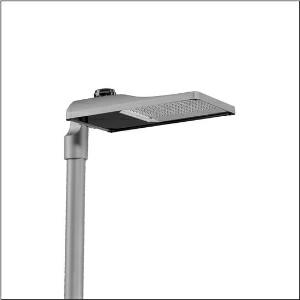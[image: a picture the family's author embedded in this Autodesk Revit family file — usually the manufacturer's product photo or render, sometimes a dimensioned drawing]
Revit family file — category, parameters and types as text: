
# Revit family: streetlight_sl_31_maxi___pl52_5xh8h75n08sa_385d
name_source: partatom
category: Lighting Fixtures
units: mm (PartAtom-declared; Revit-internal decimal feet)

## family parameters
Cut with Voids When Loaded = No
Host = Face
Light Source = No
Part Type = Normal
Room Calculation Point = No
Round Connector Dimension = Use Diameter
Shared = No

## types (1)
- --- (1 x LED, 22470 lm, 208.6 W, 2200K)
    Apparent Load = 209 VA
    CIE Flux Codes = 27 59 98 100 100
    Color Rendering = 70
    Color Temperature = 2200K
    Default Elevation = 1800 mm
    Description = Streetlight SL 31 maxi, mast luminaire, primary light control with lens, of PMMA, primary optical cover: cover, of toughened safety glass, transparent, light distribution: PL52, light emission: direct distribution, primary light characteristic: asymmetric, installation type: post-top, side-entry, LED, High Power LED, rated luminous flux: 22.470lm, luminous efficacy: 108lm/W, light colour: 722, colour temperature: 2200K, control: presetting dimming linear, flexible luminous flux parameterisation, time-dependent luminous flux control, constant luminous flux control, intelligent temperature release in ECG and LED module, overheat protection, with cable H07RN-F 3x 1.5mm², mains connection: 220..240V, AC, 50/60Hz, connection cable pre-assembled, cable length: 14,5m, start of lifetime: 209W, end of service life: 233W, reduction: 88W, luminaire housing, of diecast aluminium, powder-coated, Siteco® metallic grey (DB 702S), corrosivity category C5 high according to DIN EN ISO 12944, no sealing on luminaire upper side, inclination: -15°..+20° (post-top) | -20°..+20° (side-entry), adjustable in 5° steps, mast flange (76/60mm) included as standard, multi-level sealing system, sealing non-destructively replaceable, protection rating (complete): IP66, insulation class (complete): insulation class I (protective earthing), certification: CE, ENEC, ENEC+, VDE, UKCA, impact resistance: IK09, permissible operating ambient temperature for outdoor applications: -40..+50°C, standard-compliant lighting for roads and squares, packaging unit: 1 piece

Light Distribution: PL52
    Height = 79 mm
    Lamp = 1 x LED
    Lamp Light Flux = 22470 lm
    Lamp Power = 208.6 W
    Lamp count = 1
    Length = 657 mm
    Luminous efficacy = 108 lm/W
    Manufacturer = Siteco
    ModVariant = No
    Model = 5XH8H75N08SA
    Number of Poles = 1
    OnlyDefault = Yes
    Power Factor = 1
    Product Name = Streetlight SL 31 maxi | PL52
    Product group = mast luminaire | pylon top
    ProductGroupID = 6100
    Protection Class = Protection class I
    Protection Degree = IP 66
    RLX_Detail_Level = 1
    RLX_Emergency_Light_Flux = 0 lm
    RLX_Emergency_Type = 0
    RLX_Emergency_Type_DB = No
    RlxData = <blob elided: 57189 chars, md5=23e13f9c>
    Socket = socket
    Standby Power = 0 W
    System Light Flux = 22470 lm
    System Power = 209 W
    Type Comments = factory setting: luminous flux: 100 % | dim-lin: 254 | 718 mA
    Type Image = l_1300293.jpg
    URL = http://relux.com
    VarID = @adj_002499
    Voltage = 0 V
    Weight = 0.00 kg
    Width = 362 mm

## geometry (parser evidence)
native form markers: Blend x4, Sweep x12
no freeform markers — native parametric forms only
